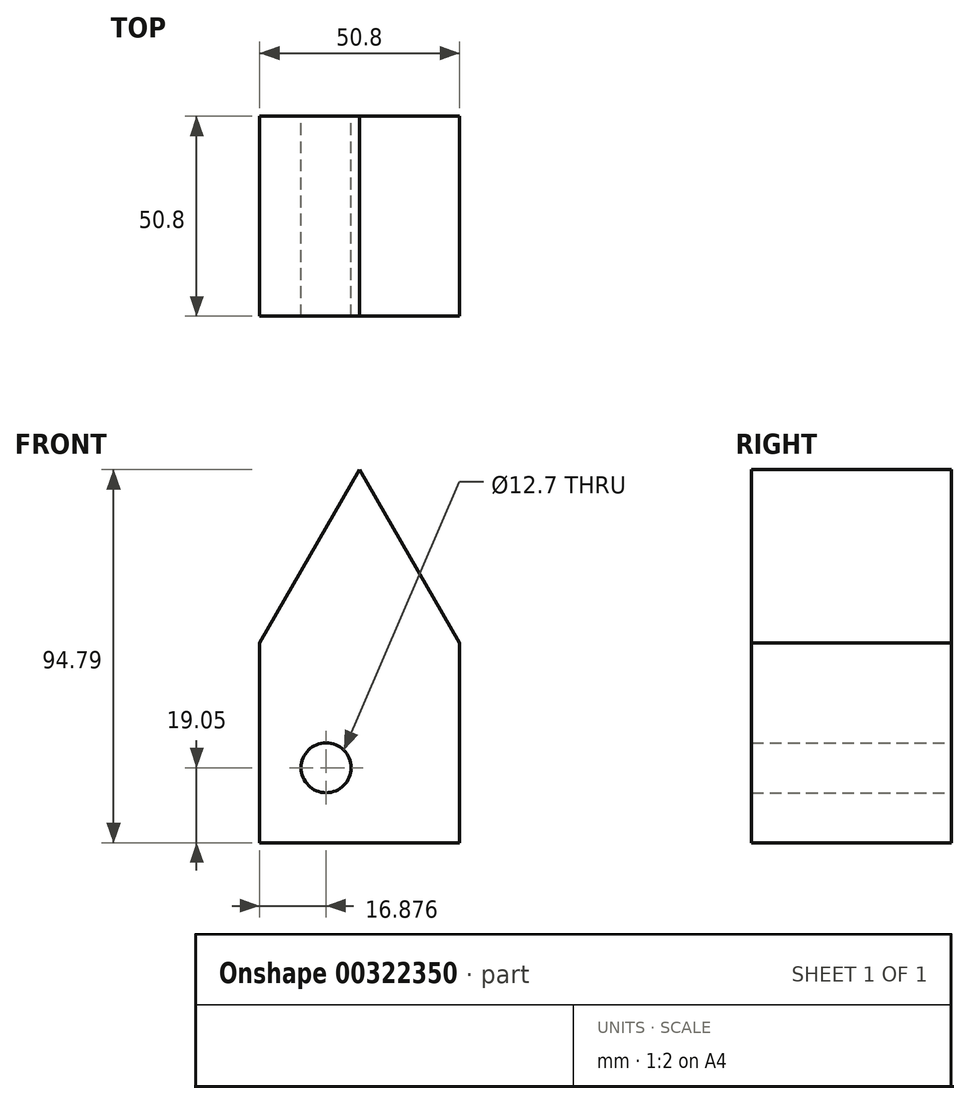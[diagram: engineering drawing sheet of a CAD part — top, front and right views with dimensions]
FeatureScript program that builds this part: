
annotation { "Feature Type Name" : "Feature", "Feature Type Description" : "" }
export const myFeature = defineFeature(function(context is Context, id is Id, definition is map)
    precondition{}
    {
        {
            var Q0;
            Q0=qCreatedBy(makeId("Front.planeOp"),FACE);
            var sketch = newSketch(context, id + "F0", { "sketchPlane" : qUnion([Q0])});
            skLineSegment(sketch, "E0.bottom", {"start": v(0, 0) * mm, "end": v(-50.8, 0) * mm});
            skLineSegment(sketch, "E0.left", {"start": v(0, 0) * mm, "end": v(0, 50.8) * mm});
            skLineSegment(sketch, "E0.right", {"start": v(-50.8, 0) * mm, "end": v(-50.8, 50.8) * mm});
            skLineSegment(sketch, "E1", {"start": v(-50.8, 50.8) * mm, "end": v(-25.4, 94.8) * mm});
            skLineSegment(sketch, "E2", {"start": v(-25.4, 94.8) * mm, "end": v(0, 50.8) * mm});
            skCircle(sketch, "E3", {"center": v(-33.92, 19.05) * mm, "radius": 6.35 * mm});
            skSolve(sketch);
        }
        {
            var Q0;
            Q0=makeQuery(id+"F0.imprint","IMPRINT",FACE,{"disambiguationData":[TD([[makeQuery(id+"F0.imprint","IMPRINT",EDGE,{"derivedFrom":sQuery(id+"F0.wireOp",EDGE,"E0.bottom")}),-1.0]])]});
            extrude(context, id + "F1", {"entities" : qUnion([Q0]), "depth" : 50.8 * mm});
        }
    });
